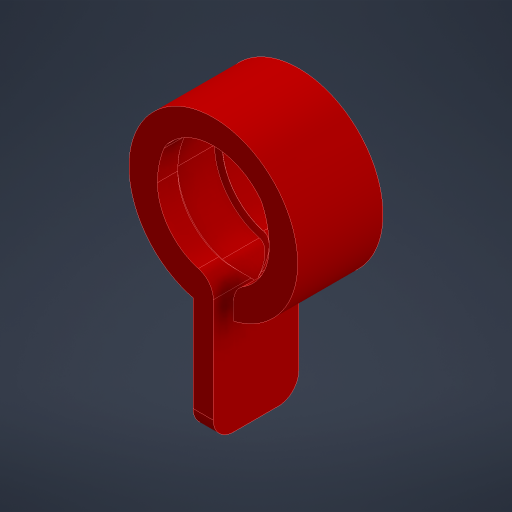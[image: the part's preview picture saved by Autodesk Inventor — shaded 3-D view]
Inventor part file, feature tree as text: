
AUTODESK INVENTOR PART (.ipt)
format: ipt  version: 2023.4 (Build 274418000, 418)  size: 342,016 bytes
history: native  units: mm
features: extrude x5, fillet x2, sketch x1, chamfer x1
ambient origin geometry x8: Origin, YZ Plane, XZ Plane, XY Plane, X Axis, Y Axis, Z Axis, Center Point
bodies: Solid1 (feature_tree)
feature tree (9):
  sketch  "Sketch1"  dims[d3=2.5mm d4=10.0mm d8=2.5mm d9=0.0mm d10=5.5mm d11=0.0mm d12=2.5mm d13=0.0mm d14=2.5mm d15=17.5mm d18=2.5mm d20=2.5mm d21=0.0mm d22=2.5mm d23=17.5mm d24=2.5mm d25=10.0mm d26=0.0mm d27=13.75mm d28=0.5mm d32=1.25mm d33=2.5mm d34=2.0mm d35=1.0mm d36=0.475mm d37=2.0mm d38=45.0deg d39=0.0mm]
  extrude  "Extrusion1"  Depth=10.0mm
  extrude  "Extrusion2"  Depth=2.5mm TaperAngle=0.0deg
  extrude  "Extrusion3"  Depth=2.5mm TaperAngle=0.0deg
  fillet  "Fillet1"  Radius=2.5mm
  extrude  "Extrusion4"  Depth=2.5mm
  extrude  "Extrusion5"  Depth=2.5mm
  chamfer  "Chamfer1"  Distance=2.5mm
  fillet  "Fillet2"  Radius=2.5mm
